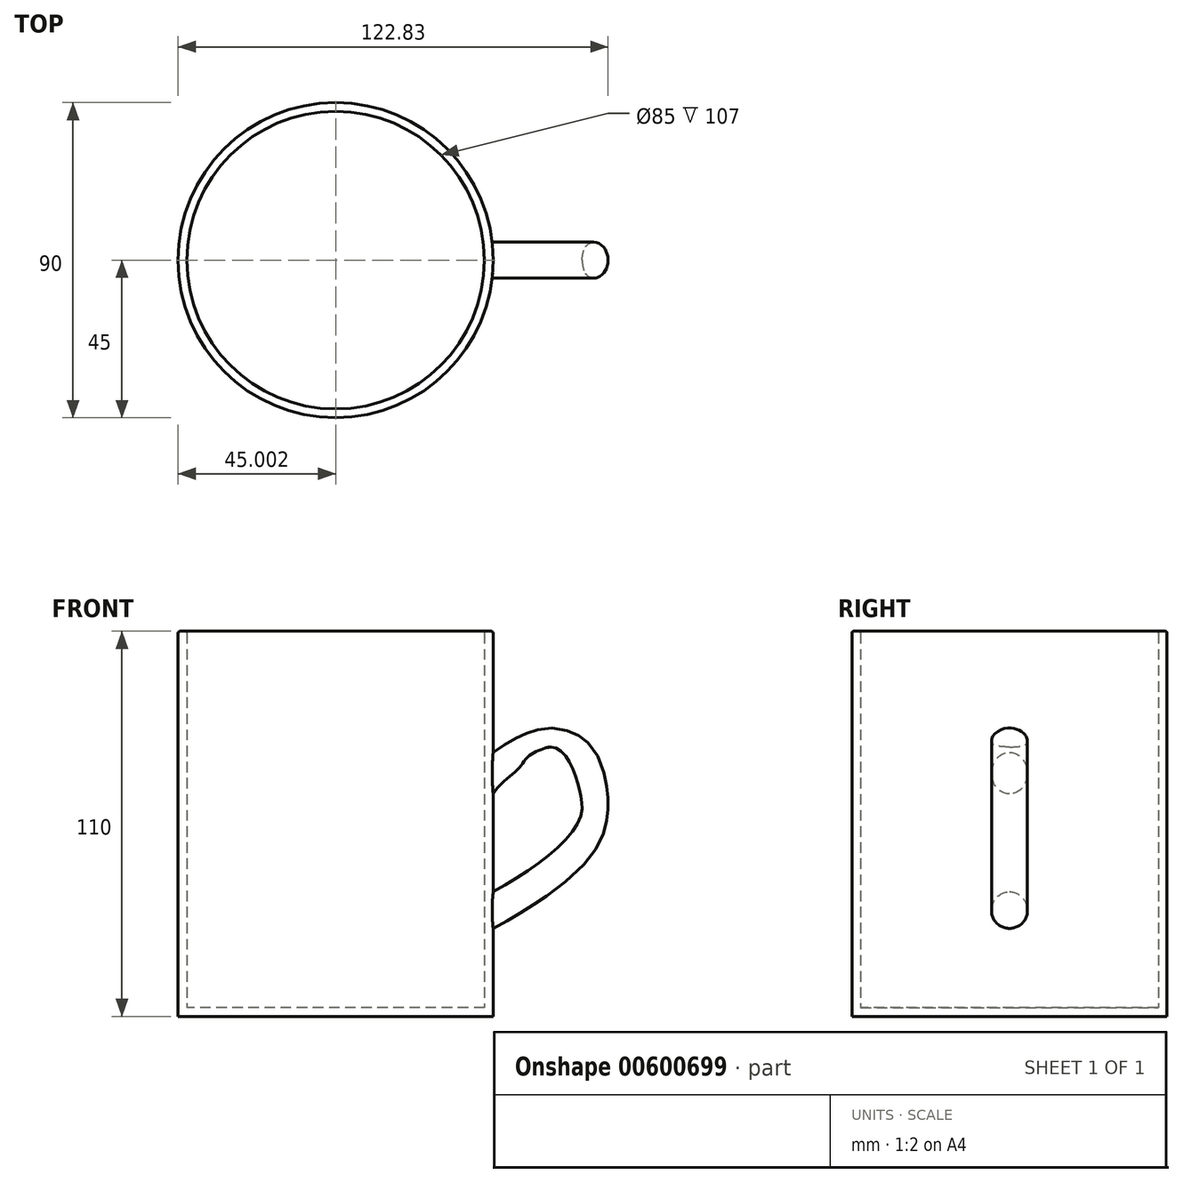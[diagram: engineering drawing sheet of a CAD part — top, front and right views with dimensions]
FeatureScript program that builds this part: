
annotation { "Feature Type Name" : "Feature", "Feature Type Description" : "" }
export const myFeature = defineFeature(function(context is Context, id is Id, definition is map)
    precondition{}
    {
        {
            var Q0;
            Q0=qCreatedBy(makeId("Top.planeOp"),FACE);
            var sketch = newSketch(context, id + "F0", { "sketchPlane" : qUnion([Q0])});
            skCircle(sketch, "E0", {"center": v(-3.55, 0) * mm, "radius": 45 * mm});
            skSolve(sketch);
        }
        {
            var Q0;
            Q0=makeQuery(id+"F0.imprint","IMPRINT",FACE,{"disambiguationData":[TD([[makeQuery(id+"F0.imprint","IMPRINT",EDGE,{"derivedFrom":sQuery(id+"F0.wireOp",EDGE,"E0")}),1.0]])]});
            extrude(context, id + "F1", {"entities" : qUnion([Q0]), "depth" : 110 * mm, "offsetDistance" : 25 * mm});
        }
        {
            var Q0;
            Q0=qCreatedBy(makeId("Front.planeOp"),FACE);
            var sketch = newSketch(context, id + "F2", { "sketchPlane" : qUnion([Q0])});
            skFitSpline(sketch, "E1", {"points": [v(35.67, 78.7) * mm, v(42.19, 83.47) * mm, v(57.2, 88.46) * mm, v(72.96, 82.4) * mm, v(80.2, 66.01) * mm, v(77.2, 46.36) * mm, v(60.25, 29.05) * mm, v(34.88, 14.35) * mm], "startDerivative": vector(59.8, 54.47) * mm, "endDerivative": vector(-144, -76.1) * mm});
            skSolve(sketch);
        }
        {
            var Q0;
            Q0=qCreatedBy(makeId("Right.planeOp"),FACE);
            cPlane(context, id + "F3", {"entities" : qUnion([Q0]), "cplaneType" : CPlaneType.OFFSET, "offset" : 45 * mm, "width" : 150 * mm, "height" : 150 * mm});
        }
        {
            var Q0;
            Q0=qCreatedBy(id+"F3.planeOp",FACE);
            var sketch = newSketch(context, id + "F4", { "sketchPlane" : qUnion([Q0])});
            skCircle(sketch, "E2", {"center": v(0, 72.67) * mm, "radius": 5.13 * mm});
            skSolve(sketch);
        }
        {
            var Q0;
            Q0=makeQuery(id+"F4.imprint","IMPRINT",FACE,{"disambiguationData":[TD([[makeQuery(id+"F4.imprint","IMPRINT",EDGE,{"derivedFrom":sQuery(id+"F4.wireOp",EDGE,"E2")}),1.0]])]});
            var Q1;
            Q1=sQuery(id+"F2.wireOp",EDGE,"E1");
            sweep(context, id + "F5", {"operationType" : NewBodyOperationType.ADD, "profiles" : qUnion([Q0]), "path" : qUnion([Q1])});
        }
        {
            var Q0;
            Q0=makeQuery(id+"F1.opExtrude","CAP_FACE",FACE,{"disambiguationData":[OSD([sQuery(id+"F0.wireOp",EDGE,"E0")])],"isStart":false});
            shell(context, id + "F6", {"entities" : qUnion([Q0]), "thickness" : 2.5 * mm});
        }
        {
            var Q0;
            Q0=makeQuery(id+"F1.opExtrude","CAP_EDGE",EDGE,{"disambiguationData":[OSD([sQuery(id+"F0.wireOp",EDGE,"E0")])],"isStart":false});
            var Q1;
            {var subQ0=sQuery(id+"F0.wireOp",EDGE,"E0");Q1=makeQuery(id+"F6.opShell","OFFSET_EDGE",EDGE,{"disambiguationData":[OSD([subQ0]),TDD([makeQuery(id+"F1.opExtrude","CAP_EDGE",EDGE,{"disambiguationData":[OSD([subQ0])],"isStart":false})])]});}
            fillet(context, id + "F7", {"entities" : qUnion([Q0, Q1]), "radius" : 0.5 * mm, "tangentPropagation" : true, "allowEdgeOverflow" : false});
        }
    });
